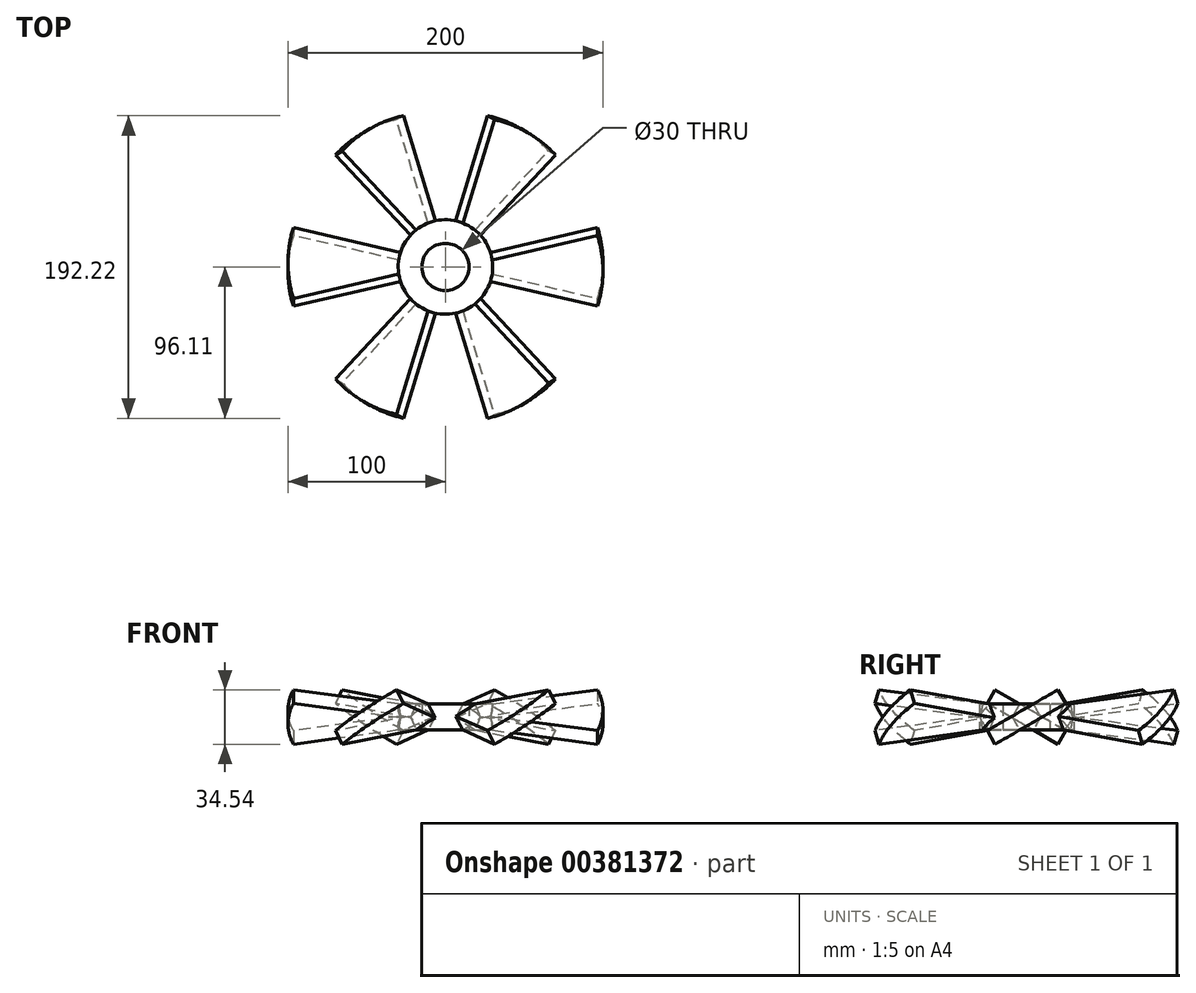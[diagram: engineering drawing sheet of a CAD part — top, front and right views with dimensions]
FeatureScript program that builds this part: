
annotation { "Feature Type Name" : "Feature", "Feature Type Description" : "" }
export const myFeature = defineFeature(function(context is Context, id is Id, definition is map)
    precondition{}
    {
        {
            var Q0;
            Q0=qCreatedBy(makeId("Top.planeOp"),FACE);
            var sketch = newSketch(context, id + "F0", { "sketchPlane" : qUnion([Q0])});
            skCircle(sketch, "E0", {"center": v(0, 0) * mm, "radius": 15 * mm});
            skCircle(sketch, "E1", {"center": v(0, 0) * mm, "radius": 30 * mm});
            skCircle(sketch, "E2", {"center": v(0, 0) * mm, "radius": 100 * mm});
            skLineSegment(sketch, "E3", {"start": v(0, 0) * mm, "end": v(96.6, 25.88) * mm});
            skLineSegment(sketch, "E4", {"start": v(0, 0) * mm, "end": v(96.6, -25.88) * mm});
            skLineSegment(sketch, "E5", {"start": v(0, 0) * mm, "end": v(100, 0) * mm, "construction": true});
            skSolve(sketch);
        }
        {
            var Q0;
            {var subQ0=sQuery(id+"F0.wireOp",EDGE,"E3");var subQ1=sQuery(id+"F0.wireOp",EDGE,"E1");var subQ2=makeQuery(id+"F0.imprint","INTERSECT",VERTEX,{"derivedFrom":[subQ1,subQ0]});Q0=makeQuery(id+"F0.imprint","IMPRINT",FACE,{"disambiguationData":[TD([[makeQuery(id+"F0.imprint","IMPRINT",EDGE,{"disambiguationData":[TD([[subQ2,1.0]])],"derivedFrom":subQ1}),-1.0]])]});}
            var Q1;
            {var subQ0=sQuery(id+"F0.wireOp",EDGE,"E3");var subQ1=sQuery(id+"F0.wireOp",EDGE,"E0");var subQ2=makeQuery(id+"F0.imprint","INTERSECT",VERTEX,{"derivedFrom":[subQ1,subQ0]});Q1=makeQuery(id+"F0.imprint","IMPRINT",FACE,{"disambiguationData":[TD([[makeQuery(id+"F0.imprint","IMPRINT",EDGE,{"disambiguationData":[TD([[subQ2,1.0]])],"derivedFrom":subQ1}),-1.0]])]});}
            extrude(context, id + "F1", {"entities" : qUnion([Q0, Q1]), "endBound" : BoundingType.SYMMETRIC, "depth" : 10 * mm});
        }
        {
            var Q0;
            Q0=qCreatedBy(makeId("Front.planeOp"),FACE);
            var sketch = newSketch(context, id + "F2", { "sketchPlane" : qUnion([Q0])});
            skLineSegment(sketch, "E6", {"start": v(0, 39.84) * mm, "end": v(0, -44.46) * mm, "construction": true});
            skSolve(sketch);
        }
        {
            var Q0;
            Q0=makeQuery(id+"F1.opExtrude","SWEPT_BODY",BODY,{"disambiguationData":[OSD([sQuery(id+"F0.wireOp",EDGE,"E1"),sQuery(id+"F0.wireOp",EDGE,"E2"),sQuery(id+"F0.wireOp",EDGE,"E3"),sQuery(id+"F0.wireOp",EDGE,"E4")])]});
            var Q1;
            Q1=sQuery(id+"F0.wireOp",EDGE,"E5");
            var Q2;
            Q2=sQuery(id+"F0.wireOp",EDGE,"E5");
            transform(context, id + "F3", {"entities" : qUnion([Q0]), "transformType" : TransformType.ROTATION, "transformAxis" : qUnion([Q2]), "angle" : 30 * degree, "makeCopy" : false});
        }
        {
            var Q0;
            Q0=makeQuery(id+"F1.opExtrude","SWEPT_BODY",BODY,{"disambiguationData":[OSD([sQuery(id+"F0.wireOp",EDGE,"E1"),sQuery(id+"F0.wireOp",EDGE,"E2"),sQuery(id+"F0.wireOp",EDGE,"E3"),sQuery(id+"F0.wireOp",EDGE,"E4")])]});
            var Q1;
            Q1=sQuery(id+"F2.wireOp",EDGE,"E6");
            transform(context, id + "F4", {"entities" : qUnion([Q0]), "transformType" : TransformType.ROTATION, "transformAxis" : qUnion([Q1]), "angle" : 60 * degree, "makeCopy" : true});
        }
        {
            var Q0;
            Q0=makeQuery(id+"F4.opPattern","COPY",BODY,{"derivedFrom":makeQuery(id+"F1.opExtrude","SWEPT_BODY",BODY,{"disambiguationData":[OSD([sQuery(id+"F0.wireOp",EDGE,"E1"),sQuery(id+"F0.wireOp",EDGE,"E2"),sQuery(id+"F0.wireOp",EDGE,"E3"),sQuery(id+"F0.wireOp",EDGE,"E4")])]}),"instanceName":"1"});
            var Q1;
            Q1=sQuery(id+"F2.wireOp",EDGE,"E6");
            transform(context, id + "F5", {"entities" : qUnion([Q0]), "transformType" : TransformType.ROTATION, "transformAxis" : qUnion([Q1]), "angle" : 60 * degree, "makeCopy" : true});
        }
        {
            var Q0;
            Q0=makeQuery(id+"F5.opPattern","COPY",BODY,{"derivedFrom":makeQuery(id+"F4.opPattern","COPY",BODY,{"derivedFrom":makeQuery(id+"F1.opExtrude","SWEPT_BODY",BODY,{"disambiguationData":[OSD([sQuery(id+"F0.wireOp",EDGE,"E1"),sQuery(id+"F0.wireOp",EDGE,"E2"),sQuery(id+"F0.wireOp",EDGE,"E3"),sQuery(id+"F0.wireOp",EDGE,"E4")])]}),"instanceName":"1"}),"instanceName":"1"});
            var Q1;
            Q1=sQuery(id+"F2.wireOp",EDGE,"E6");
            transform(context, id + "F6", {"entities" : qUnion([Q0]), "transformType" : TransformType.ROTATION, "transformAxis" : qUnion([Q1]), "angle" : 60 * degree, "makeCopy" : true});
        }
        {
            var Q0;
            Q0=makeQuery(id+"F6.opPattern","COPY",BODY,{"derivedFrom":makeQuery(id+"F5.opPattern","COPY",BODY,{"derivedFrom":makeQuery(id+"F4.opPattern","COPY",BODY,{"derivedFrom":makeQuery(id+"F1.opExtrude","SWEPT_BODY",BODY,{"disambiguationData":[OSD([sQuery(id+"F0.wireOp",EDGE,"E1"),sQuery(id+"F0.wireOp",EDGE,"E2"),sQuery(id+"F0.wireOp",EDGE,"E3"),sQuery(id+"F0.wireOp",EDGE,"E4")])]}),"instanceName":"1"}),"instanceName":"1"}),"instanceName":"1"});
            var Q1;
            Q1=sQuery(id+"F2.wireOp",EDGE,"E6");
            transform(context, id + "F7", {"entities" : qUnion([Q0]), "transformType" : TransformType.ROTATION, "transformAxis" : qUnion([Q1]), "angle" : 60 * degree, "makeCopy" : true});
        }
        {
            var Q0;
            Q0=makeQuery(id+"F7.opPattern","COPY",BODY,{"derivedFrom":makeQuery(id+"F6.opPattern","COPY",BODY,{"derivedFrom":makeQuery(id+"F5.opPattern","COPY",BODY,{"derivedFrom":makeQuery(id+"F4.opPattern","COPY",BODY,{"derivedFrom":makeQuery(id+"F1.opExtrude","SWEPT_BODY",BODY,{"disambiguationData":[OSD([sQuery(id+"F0.wireOp",EDGE,"E1"),sQuery(id+"F0.wireOp",EDGE,"E2"),sQuery(id+"F0.wireOp",EDGE,"E3"),sQuery(id+"F0.wireOp",EDGE,"E4")])]}),"instanceName":"1"}),"instanceName":"1"}),"instanceName":"1"}),"instanceName":"1"});
            var Q1;
            Q1=sQuery(id+"F2.wireOp",EDGE,"E6");
            transform(context, id + "F8", {"entities" : qUnion([Q0]), "transformType" : TransformType.ROTATION, "transformAxis" : qUnion([Q1]), "angle" : 60 * degree, "makeCopy" : true});
        }
        {
            var Q0;
            {var subQ0=sQuery(id+"F0.wireOp",EDGE,"E3");var subQ1=sQuery(id+"F0.wireOp",EDGE,"E0");var subQ2=makeQuery(id+"F0.imprint","INTERSECT",VERTEX,{"derivedFrom":[subQ1,subQ0]});Q0=makeQuery(id+"F0.imprint","IMPRINT",FACE,{"disambiguationData":[TD([[makeQuery(id+"F0.imprint","IMPRINT",EDGE,{"disambiguationData":[TD([[subQ2,1.0]])],"derivedFrom":subQ1}),-1.0]])]});}
            var Q1;
            {var subQ0=sQuery(id+"F0.wireOp",EDGE,"E3");var subQ1=sQuery(id+"F0.wireOp",EDGE,"E0");var subQ2=makeQuery(id+"F0.imprint","INTERSECT",VERTEX,{"derivedFrom":[subQ1,subQ0]});Q1=makeQuery(id+"F0.imprint","IMPRINT",FACE,{"disambiguationData":[TD([[makeQuery(id+"F0.imprint","IMPRINT",EDGE,{"disambiguationData":[TD([[subQ2,-1.0]])],"derivedFrom":subQ1}),-1.0]])]});}
            extrude(context, id + "F9", {"entities" : qUnion([Q0, Q1]), "endBound" : BoundingType.SYMMETRIC, "depth" : 25 * mm});
        }
        {
            var Q0;
            Q0=qCreatedBy(makeId("Top.planeOp"),FACE);
            var sketch = newSketch(context, id + "F10", { "sketchPlane" : qUnion([Q0])});
            skCircle(sketch, "E7", {"center": v(0, 0) * mm, "radius": 15 * mm});
            skSolve(sketch);
        }
        {
            var Q0;
            Q0 = qSketchRegion(id + "F10", true);
            extrude(context, id + "F11", {"entities" : qUnion([Q0]), "endBound" : BoundingType.SYMMETRIC, "depth" : 25 * mm});
        }
        {
            var Q0;
            Q0=makeQuery(id+"F9.opExtrude","SWEPT_BODY",BODY,{"disambiguationData":[OSD([sQuery(id+"F0.wireOp",EDGE,"E0"),sQuery(id+"F0.wireOp",EDGE,"E1")])]});
            var Q1;
            Q1=makeQuery(id+"F11.opExtrude","SWEPT_BODY",BODY,{"disambiguationData":[OSD([sQuery(id+"F10.wireOp",EDGE,"E7")])]});
            booleanBodies(context, id + "F12", {"operationType" : BooleanOperationType.UNION, "tools" : qUnion([Q0, Q1])});
        }
        {
            var Q0;
            Q0=makeQuery(id+"F1.opExtrude","SWEPT_BODY",BODY,{"disambiguationData":[OSD([sQuery(id+"F0.wireOp",EDGE,"E0"),sQuery(id+"F0.wireOp",EDGE,"E2"),sQuery(id+"F0.wireOp",EDGE,"E3"),sQuery(id+"F0.wireOp",EDGE,"E4")])]});
            var Q1;
            Q1=makeQuery(id+"F4.opPattern","COPY",BODY,{"derivedFrom":makeQuery(id+"F1.opExtrude","SWEPT_BODY",BODY,{"disambiguationData":[OSD([sQuery(id+"F0.wireOp",EDGE,"E0"),sQuery(id+"F0.wireOp",EDGE,"E2"),sQuery(id+"F0.wireOp",EDGE,"E3"),sQuery(id+"F0.wireOp",EDGE,"E4")])]}),"instanceName":"1"});
            var Q2;
            Q2=makeQuery(id+"F5.opPattern","COPY",BODY,{"derivedFrom":makeQuery(id+"F4.opPattern","COPY",BODY,{"derivedFrom":makeQuery(id+"F1.opExtrude","SWEPT_BODY",BODY,{"disambiguationData":[OSD([sQuery(id+"F0.wireOp",EDGE,"E0"),sQuery(id+"F0.wireOp",EDGE,"E2"),sQuery(id+"F0.wireOp",EDGE,"E3"),sQuery(id+"F0.wireOp",EDGE,"E4")])]}),"instanceName":"1"}),"instanceName":"1"});
            var Q3;
            Q3=makeQuery(id+"F6.opPattern","COPY",BODY,{"derivedFrom":makeQuery(id+"F5.opPattern","COPY",BODY,{"derivedFrom":makeQuery(id+"F4.opPattern","COPY",BODY,{"derivedFrom":makeQuery(id+"F1.opExtrude","SWEPT_BODY",BODY,{"disambiguationData":[OSD([sQuery(id+"F0.wireOp",EDGE,"E0"),sQuery(id+"F0.wireOp",EDGE,"E2"),sQuery(id+"F0.wireOp",EDGE,"E3"),sQuery(id+"F0.wireOp",EDGE,"E4")])]}),"instanceName":"1"}),"instanceName":"1"}),"instanceName":"1"});
            var Q4;
            Q4=makeQuery(id+"F7.opPattern","COPY",BODY,{"derivedFrom":makeQuery(id+"F6.opPattern","COPY",BODY,{"derivedFrom":makeQuery(id+"F5.opPattern","COPY",BODY,{"derivedFrom":makeQuery(id+"F4.opPattern","COPY",BODY,{"derivedFrom":makeQuery(id+"F1.opExtrude","SWEPT_BODY",BODY,{"disambiguationData":[OSD([sQuery(id+"F0.wireOp",EDGE,"E0"),sQuery(id+"F0.wireOp",EDGE,"E2"),sQuery(id+"F0.wireOp",EDGE,"E3"),sQuery(id+"F0.wireOp",EDGE,"E4")])]}),"instanceName":"1"}),"instanceName":"1"}),"instanceName":"1"}),"instanceName":"1"});
            var Q5;
            Q5=makeQuery(id+"F8.opPattern","COPY",BODY,{"derivedFrom":makeQuery(id+"F7.opPattern","COPY",BODY,{"derivedFrom":makeQuery(id+"F6.opPattern","COPY",BODY,{"derivedFrom":makeQuery(id+"F5.opPattern","COPY",BODY,{"derivedFrom":makeQuery(id+"F4.opPattern","COPY",BODY,{"derivedFrom":makeQuery(id+"F1.opExtrude","SWEPT_BODY",BODY,{"disambiguationData":[OSD([sQuery(id+"F0.wireOp",EDGE,"E0"),sQuery(id+"F0.wireOp",EDGE,"E2"),sQuery(id+"F0.wireOp",EDGE,"E3"),sQuery(id+"F0.wireOp",EDGE,"E4")])]}),"instanceName":"1"}),"instanceName":"1"}),"instanceName":"1"}),"instanceName":"1"}),"instanceName":"1"});
            var Q6;
            Q6=makeQuery(id+"F9.opExtrude","SWEPT_BODY",BODY,{"disambiguationData":[OSD([sQuery(id+"F0.wireOp",EDGE,"E0"),sQuery(id+"F0.wireOp",EDGE,"E1")])]});
            booleanBodies(context, id + "F13", {"operationType" : BooleanOperationType.UNION, "tools" : qUnion([Q0, Q1, Q2, Q3, Q4, Q5, Q6])});
        }
        {
            var Q0;
            {var subQ0=sQuery(id+"F0.wireOp",EDGE,"E3");Q0=makeQuery(id+"F13.opBoolean","INTERSECT",VERTEX,{"derivedFrom":[makeQuery(id+"F4.opPattern","COPY",FACE,{"derivedFrom":makeQuery(id+"F1.opExtrude","CAP_FACE",FACE,{"disambiguationData":[OSD([sQuery(id+"F0.wireOp",EDGE,"E0"),sQuery(id+"F0.wireOp",EDGE,"E2"),subQ0,sQuery(id+"F0.wireOp",EDGE,"E4")])],"isStart":false}),"instanceName":"1"}),makeQuery(id+"F4.opPattern","COPY",FACE,{"derivedFrom":makeQuery(id+"F1.opExtrude","SWEPT_FACE",FACE,{"disambiguationData":[OSD([subQ0])]}),"instanceName":"1"}),makeQuery(id+"F9.opExtrude","SWEPT_FACE",FACE,{"disambiguationData":[OSD([sQuery(id+"F0.wireOp",EDGE,"E1")])]})]});}
            var Q1;
            {var subQ0=sQuery(id+"F0.wireOp",EDGE,"E3");Q1=makeQuery(id+"F13.opBoolean","INTERSECT",VERTEX,{"derivedFrom":[makeQuery(id+"F5.opPattern","COPY",FACE,{"derivedFrom":makeQuery(id+"F4.opPattern","COPY",FACE,{"derivedFrom":makeQuery(id+"F1.opExtrude","CAP_FACE",FACE,{"disambiguationData":[OSD([sQuery(id+"F0.wireOp",EDGE,"E0"),sQuery(id+"F0.wireOp",EDGE,"E2"),subQ0,sQuery(id+"F0.wireOp",EDGE,"E4")])],"isStart":false}),"instanceName":"1"}),"instanceName":"1"}),makeQuery(id+"F5.opPattern","COPY",FACE,{"derivedFrom":makeQuery(id+"F4.opPattern","COPY",FACE,{"derivedFrom":makeQuery(id+"F1.opExtrude","SWEPT_FACE",FACE,{"disambiguationData":[OSD([subQ0])]}),"instanceName":"1"}),"instanceName":"1"}),makeQuery(id+"F9.opExtrude","SWEPT_FACE",FACE,{"disambiguationData":[OSD([sQuery(id+"F0.wireOp",EDGE,"E1")])]})]});}
            var Q2;
            {var subQ0=sQuery(id+"F0.wireOp",EDGE,"E3");Q2=makeQuery(id+"F13.opBoolean","INTERSECT",VERTEX,{"derivedFrom":[makeQuery(id+"F6.opPattern","COPY",FACE,{"derivedFrom":makeQuery(id+"F5.opPattern","COPY",FACE,{"derivedFrom":makeQuery(id+"F4.opPattern","COPY",FACE,{"derivedFrom":makeQuery(id+"F1.opExtrude","CAP_FACE",FACE,{"disambiguationData":[OSD([sQuery(id+"F0.wireOp",EDGE,"E0"),sQuery(id+"F0.wireOp",EDGE,"E2"),subQ0,sQuery(id+"F0.wireOp",EDGE,"E4")])],"isStart":false}),"instanceName":"1"}),"instanceName":"1"}),"instanceName":"1"}),makeQuery(id+"F6.opPattern","COPY",FACE,{"derivedFrom":makeQuery(id+"F5.opPattern","COPY",FACE,{"derivedFrom":makeQuery(id+"F4.opPattern","COPY",FACE,{"derivedFrom":makeQuery(id+"F1.opExtrude","SWEPT_FACE",FACE,{"disambiguationData":[OSD([subQ0])]}),"instanceName":"1"}),"instanceName":"1"}),"instanceName":"1"}),makeQuery(id+"F9.opExtrude","SWEPT_FACE",FACE,{"disambiguationData":[OSD([sQuery(id+"F0.wireOp",EDGE,"E1")])]})]});}
            cPlane(context, id + "F14", {"entities" : qUnion([Q0, Q1, Q2]), "cplaneType" : CPlaneType.THREE_POINT, "offset" : 25 * mm, "width" : 150 * mm, "height" : 150 * mm});
        }
        {
            var Q0;
            Q0=qCreatedBy(id+"F14.planeOp",FACE);
            var sketch = newSketch(context, id + "F15", { "sketchPlane" : qUnion([Q0])});
            skCircle(sketch, "E8", {"center": v(0, 0) * mm, "radius": 30 * mm});
            skSolve(sketch);
        }
        {
            var Q0;
            Q0=makeQuery(id+"F12.opBoolean","MERGE",FACE,{"derivedFrom":[makeQuery(id+"F9.opExtrude","CAP_FACE",FACE,{"disambiguationData":[OSD([sQuery(id+"F0.wireOp",EDGE,"E0"),sQuery(id+"F0.wireOp",EDGE,"E1")])],"isStart":false}),makeQuery(id+"F11.opExtrude","CAP_FACE",FACE,{"disambiguationData":[OSD([sQuery(id+"F10.wireOp",EDGE,"E7")])],"isStart":false})]});
            var Q1;
            Q1=sQuery(id+"F15.wireOp",EDGE,"E8");
            var Q2;
            Q2=qCreatedBy(id+"F14.planeOp",FACE);
            extrude(context, id + "F16", {"entities" : qUnion([Q0]), "operationType" : NewBodyOperationType.REMOVE, "surfaceEntities" : qUnion([Q1]), "endBound" : BoundingType.UP_TO_SURFACE, "oppositeDirection" : true, "endBoundEntityFace" : qUnion([Q2]), "depth" : 25 * mm});
        }
        {
            var Q0;
            {var subQ0=sQuery(id+"F0.wireOp",EDGE,"E4");Q0=makeQuery(id+"F13.opBoolean","INTERSECT",VERTEX,{"derivedFrom":[makeQuery(id+"F8.opPattern","COPY",FACE,{"derivedFrom":makeQuery(id+"F7.opPattern","COPY",FACE,{"derivedFrom":makeQuery(id+"F6.opPattern","COPY",FACE,{"derivedFrom":makeQuery(id+"F5.opPattern","COPY",FACE,{"derivedFrom":makeQuery(id+"F4.opPattern","COPY",FACE,{"derivedFrom":makeQuery(id+"F1.opExtrude","CAP_FACE",FACE,{"disambiguationData":[OSD([sQuery(id+"F0.wireOp",EDGE,"E0"),sQuery(id+"F0.wireOp",EDGE,"E2"),sQuery(id+"F0.wireOp",EDGE,"E3"),subQ0])],"isStart":true}),"instanceName":"1"}),"instanceName":"1"}),"instanceName":"1"}),"instanceName":"1"}),"instanceName":"1"}),makeQuery(id+"F8.opPattern","COPY",FACE,{"derivedFrom":makeQuery(id+"F7.opPattern","COPY",FACE,{"derivedFrom":makeQuery(id+"F6.opPattern","COPY",FACE,{"derivedFrom":makeQuery(id+"F5.opPattern","COPY",FACE,{"derivedFrom":makeQuery(id+"F4.opPattern","COPY",FACE,{"derivedFrom":makeQuery(id+"F1.opExtrude","SWEPT_FACE",FACE,{"disambiguationData":[OSD([subQ0])]}),"instanceName":"1"}),"instanceName":"1"}),"instanceName":"1"}),"instanceName":"1"}),"instanceName":"1"}),makeQuery(id+"F9.opExtrude","SWEPT_FACE",FACE,{"disambiguationData":[OSD([sQuery(id+"F0.wireOp",EDGE,"E1")])]})]});}
            var Q1;
            {var subQ0=sQuery(id+"F0.wireOp",EDGE,"E4");Q1=makeQuery(id+"F13.opBoolean","INTERSECT",VERTEX,{"derivedFrom":[makeQuery(id+"F7.opPattern","COPY",FACE,{"derivedFrom":makeQuery(id+"F6.opPattern","COPY",FACE,{"derivedFrom":makeQuery(id+"F5.opPattern","COPY",FACE,{"derivedFrom":makeQuery(id+"F4.opPattern","COPY",FACE,{"derivedFrom":makeQuery(id+"F1.opExtrude","CAP_FACE",FACE,{"disambiguationData":[OSD([sQuery(id+"F0.wireOp",EDGE,"E0"),sQuery(id+"F0.wireOp",EDGE,"E2"),sQuery(id+"F0.wireOp",EDGE,"E3"),subQ0])],"isStart":true}),"instanceName":"1"}),"instanceName":"1"}),"instanceName":"1"}),"instanceName":"1"}),makeQuery(id+"F7.opPattern","COPY",FACE,{"derivedFrom":makeQuery(id+"F6.opPattern","COPY",FACE,{"derivedFrom":makeQuery(id+"F5.opPattern","COPY",FACE,{"derivedFrom":makeQuery(id+"F4.opPattern","COPY",FACE,{"derivedFrom":makeQuery(id+"F1.opExtrude","SWEPT_FACE",FACE,{"disambiguationData":[OSD([subQ0])]}),"instanceName":"1"}),"instanceName":"1"}),"instanceName":"1"}),"instanceName":"1"}),makeQuery(id+"F9.opExtrude","SWEPT_FACE",FACE,{"disambiguationData":[OSD([sQuery(id+"F0.wireOp",EDGE,"E1")])]})]});}
            var Q2;
            {var subQ0=sQuery(id+"F0.wireOp",EDGE,"E4");Q2=makeQuery(id+"F13.opBoolean","INTERSECT",VERTEX,{"derivedFrom":[makeQuery(id+"F6.opPattern","COPY",FACE,{"derivedFrom":makeQuery(id+"F5.opPattern","COPY",FACE,{"derivedFrom":makeQuery(id+"F4.opPattern","COPY",FACE,{"derivedFrom":makeQuery(id+"F1.opExtrude","CAP_FACE",FACE,{"disambiguationData":[OSD([sQuery(id+"F0.wireOp",EDGE,"E0"),sQuery(id+"F0.wireOp",EDGE,"E2"),sQuery(id+"F0.wireOp",EDGE,"E3"),subQ0])],"isStart":true}),"instanceName":"1"}),"instanceName":"1"}),"instanceName":"1"}),makeQuery(id+"F6.opPattern","COPY",FACE,{"derivedFrom":makeQuery(id+"F5.opPattern","COPY",FACE,{"derivedFrom":makeQuery(id+"F4.opPattern","COPY",FACE,{"derivedFrom":makeQuery(id+"F1.opExtrude","SWEPT_FACE",FACE,{"disambiguationData":[OSD([subQ0])]}),"instanceName":"1"}),"instanceName":"1"}),"instanceName":"1"}),makeQuery(id+"F9.opExtrude","SWEPT_FACE",FACE,{"disambiguationData":[OSD([sQuery(id+"F0.wireOp",EDGE,"E1")])]})]});}
            cPlane(context, id + "F17", {"entities" : qUnion([Q0, Q1, Q2]), "cplaneType" : CPlaneType.THREE_POINT, "offset" : 25 * mm, "width" : 150 * mm, "height" : 150 * mm});
        }
        {
            var Q0;
            Q0=makeQuery(id+"F12.opBoolean","MERGE",FACE,{"derivedFrom":[makeQuery(id+"F9.opExtrude","CAP_FACE",FACE,{"disambiguationData":[OSD([sQuery(id+"F0.wireOp",EDGE,"E0"),sQuery(id+"F0.wireOp",EDGE,"E1")])],"isStart":true}),makeQuery(id+"F11.opExtrude","CAP_FACE",FACE,{"disambiguationData":[OSD([sQuery(id+"F10.wireOp",EDGE,"E7")])],"isStart":true})]});
            var Q1;
            Q1=qCreatedBy(id+"F17.planeOp",FACE);
            extrude(context, id + "F18", {"entities" : qUnion([Q0]), "operationType" : NewBodyOperationType.REMOVE, "endBound" : BoundingType.UP_TO_SURFACE, "oppositeDirection" : true, "endBoundEntityFace" : qUnion([Q1]), "depth" : 25 * mm});
        }
        {
            var Q0;
            Q0=makeQuery(id+"F18.boolean.opBoolean","COPY",FACE,{"derivedFrom":makeQuery(id+"F18.opExtrude","CAP_FACE",FACE,{"disambiguationData":[OSD([sQuery(id+"F0.wireOp",EDGE,"E0"),sQuery(id+"F0.wireOp",EDGE,"E1"),sQuery(id+"F10.wireOp",EDGE,"E7")])],"isStart":false})});
            var sketch = newSketch(context, id + "F19", { "sketchPlane" : qUnion([Q0])});
            skCircle(sketch, "E9", {"center": v(0, 0) * mm, "radius": 15 * mm});
            skSolve(sketch);
        }
        {
            var Q0;
            Q0=makeQuery(id+"F19.imprint","IMPRINT",FACE,{"disambiguationData":[TD([[makeQuery(id+"F19.imprint","IMPRINT",EDGE,{"derivedFrom":sQuery(id+"F19.wireOp",EDGE,"E9")}),1.0]])]});
            extrude(context, id + "F20", {"entities" : qUnion([Q0]), "operationType" : NewBodyOperationType.REMOVE, "endBound" : BoundingType.UP_TO_NEXT, "oppositeDirection" : true, "depth" : 25 * mm});
        }
    });
